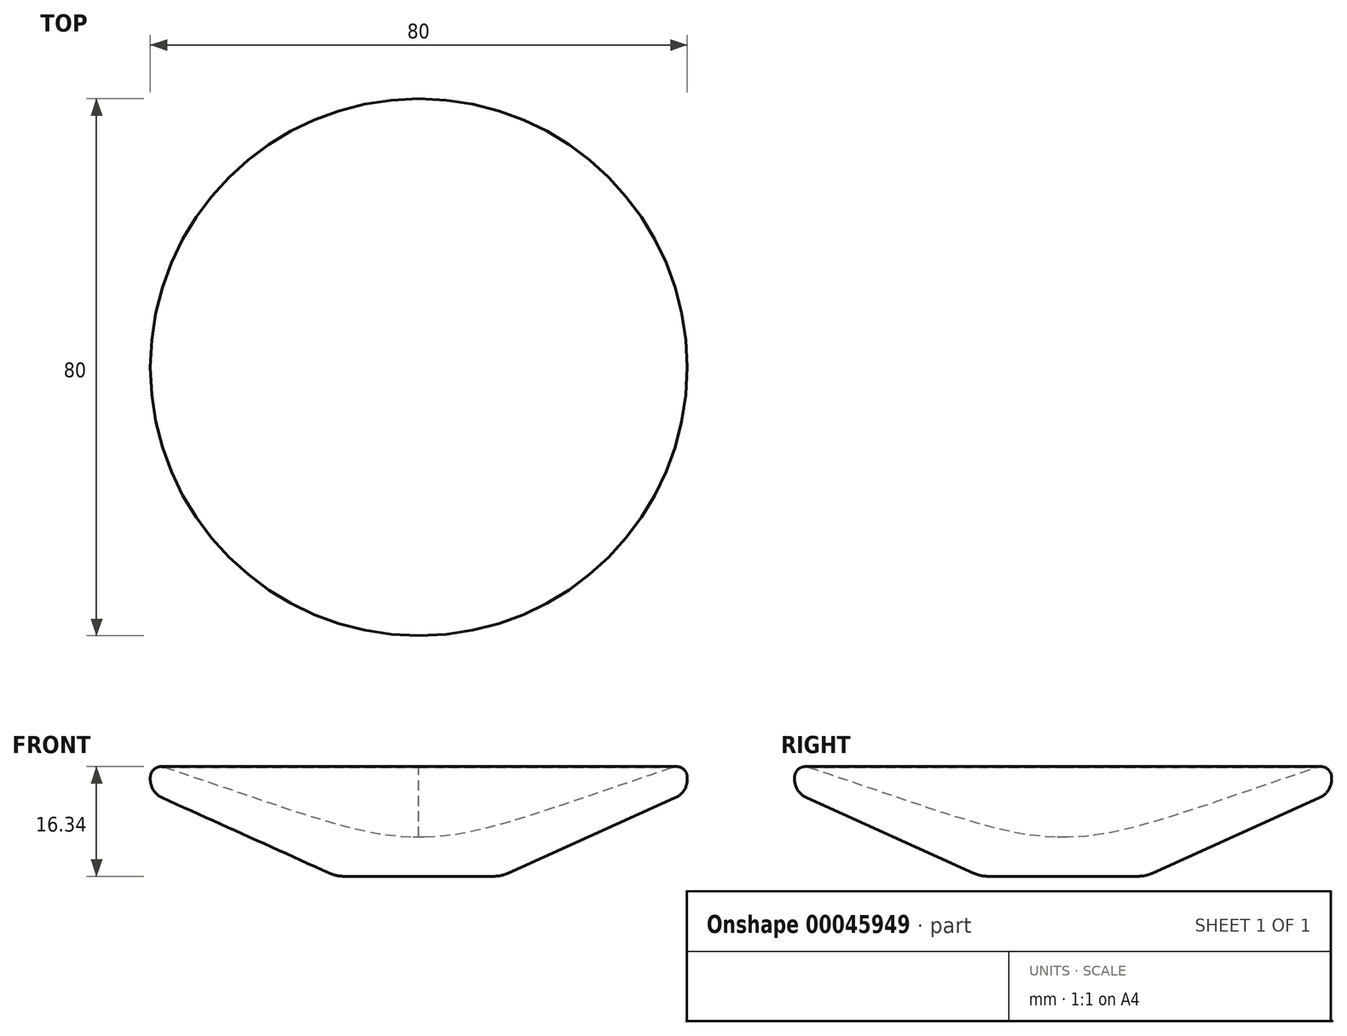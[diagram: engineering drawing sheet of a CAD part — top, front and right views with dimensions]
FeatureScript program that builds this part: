
annotation { "Feature Type Name" : "Feature", "Feature Type Description" : "" }
export const myFeature = defineFeature(function(context is Context, id is Id, definition is map)
    precondition{}
    {
        {
            var Q0;
            Q0=qCreatedBy(makeId("Right.planeOp"),FACE);
            var sketch = newSketch(context, id + "F0", { "sketchPlane" : qUnion([Q0])});
            skLineSegment(sketch, "E0", {"start": v(0, 0) * mm, "end": v(0, 41.24) * mm, "construction": true});
            skLineSegment(sketch, "E1", {"start": v(0, 0) * mm, "end": v(11.2, 0) * mm});
            skLineSegment(sketch, "E2", {"start": v(13.26, 0.44) * mm, "end": v(38.23, 11.7) * mm});
            skLineSegment(sketch, "E3", {"start": v(40, 14.43) * mm, "end": v(40, 14.75) * mm});
            skLineSegment(sketch, "E4", {"start": v(0, 0) * mm, "end": v(0, 5.92) * mm});
            skFitSpline(sketch, "E5", {"points": [v(0, 5.92) * mm, v(40, 16.94) * mm], "startDerivative": vector(26.45, -1.02) * mm, "endDerivative": vector(59.2, 19.28) * mm});
            skArc(sketch, "E6.filletArc", {"start": v(40, 14.75) * mm, "mid": v(39.34, 16.03) * mm, "end": v(37.92, 16.26) * mm});
            skPoint(sketch, "E7.visualSharp", {"position": v(40, 12.5) * mm});
            skArc(sketch, "E7.filletArc", {"start": v(38.23, 11.7) * mm, "mid": v(39.52, 12.8) * mm, "end": v(40, 14.43) * mm});
            skPoint(sketch, "E8.visualSharp", {"position": v(12.28, 0) * mm});
            skArc(sketch, "E8.filletArc", {"start": v(11.2, 0) * mm, "mid": v(12.25, 0.11) * mm, "end": v(13.26, 0.44) * mm});
            skSolve(sketch);
        }
        {
            var Q0;
            Q0 = qSketchRegion(id + "F0", true);
            var Q1;
            Q1=sQuery(id+"F0.wireOp",EDGE,"E0");
            revolve(context, id + "F1", {"entities" : qUnion([Q0]), "axis" : qUnion([Q1]), "revolveType" : RevolveType.FULL});
        }
    });
